# Revit family: Haworth_XSeries_Wardrobe
name_source: partatom
category: Furniture Systems
revit_build: Autodesk Revit 2018 (Build: 20170223_1515(x64)
units: mm (PartAtom-declared; Revit-internal decimal feet)

## family parameters
Always vertical = Yes
Cut with Voids When Loaded = No
OmniClass Number = 23.40.70.14.64.21
OmniClass Title = Systems Furniture
Part Type = Normal
Room Calculation Point = No
Round Connector Dimension = Use Diameter
Shared = No
Work Plane-Based = No

## types (4) — shared parameters
Actual Depth = 18 3/4"
Actual Width = 35 7/8"
Assembly Code = E2020200
Bar Pull = No
Classic Pull = No
Crescent Pull = No
Custom Size = No
Description = Haworth XSeries Storage Cabinet
Door Width = 17 3/16"
Doors = Yes
J Pull = No
Linear Pull = Yes
Manufacturer = Haworth
Max # of Shelves = 4
Max. Height = 63 1/2"
Max. Width = 47 7/8"
Min. Height = 27 1/2"
Min. Width = 29 7/8"
Model = JSPY
Pull Ellipse = No
Pull Finish = Haworth _ Metal _ Brushed Aluminum
Radius Pull = No
Revision Number = 6
Shelf Depth = 17 1/4"
Shelf Width = 34 3/8"
Size = Verify Final Dim. w/ Haworth
Standard Widths = 30, 36, 42 in.
Sustainability Info = https://www.haworth.com
Taper Pull = No
URL = http://www.haworth.com
URL - Product = https://www.haworth.com
Warranty = http://www.haworth.com
Width = 36"

## per-type parameters (varying)
| type | # of Shelves | Actaul # of Shelves | Actual Height | Cabinet Height | Door Height | Pull Height | Shelf Spacing | Shelves | Single Shelf |
| 18d 36w 39h | 2 | 2 | 39 1/2" | 39 1/2" | 36 3/8" | 18 3/16" | 12 1/8" | Yes | No |
| 18d 36w 27h | 1 | 2 | 27 1/2" | 27 1/2" | 24 3/8" | 12 3/16" | 8 1/8" | No | Yes |
| 18d 36w 51h | 3 | 3 | 51 1/2" | 51 1/2" | 48 3/8" | 24 3/16" | 12 3/32" | Yes | No |
| 18d 36w 63h | 4 | 4 | 63 1/2" | 63 1/2" | 60 3/8" | 30 3/16" | 12 19/256" | Yes | No |

## geometry (parser evidence)
native form markers: Sweep x9
no freeform markers — native parametric forms only
